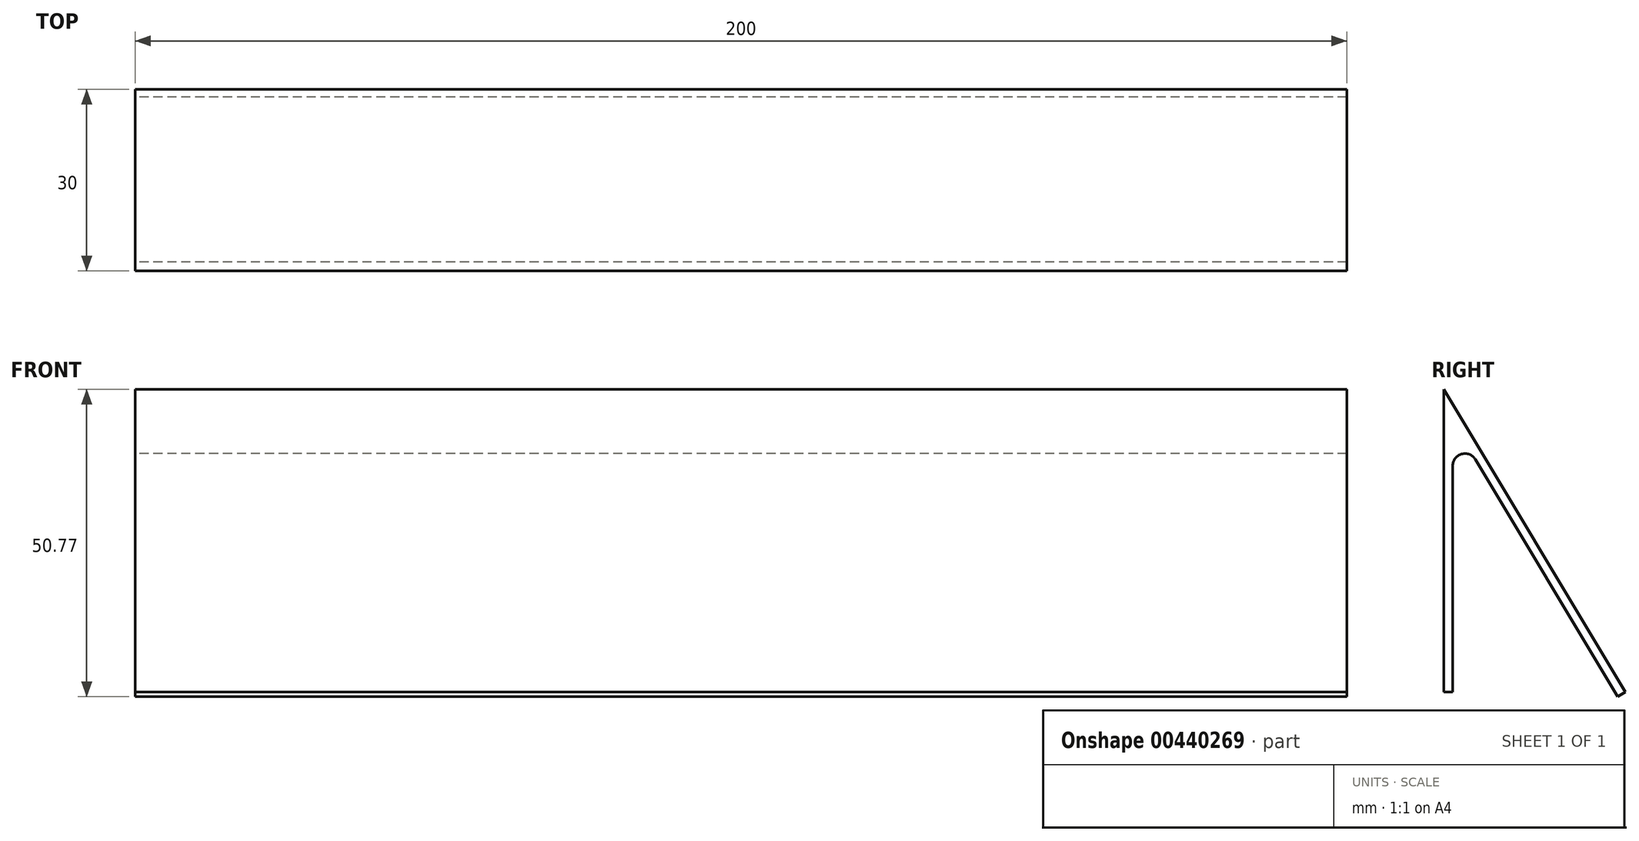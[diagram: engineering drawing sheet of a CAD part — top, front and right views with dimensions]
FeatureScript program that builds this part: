
annotation { "Feature Type Name" : "Feature", "Feature Type Description" : "" }
export const myFeature = defineFeature(function(context is Context, id is Id, definition is map)
    precondition{}
    {
        {
            var Q0;
            Q0=qCreatedBy(makeId("Right.planeOp"),FACE);
            var sketch = newSketch(context, id + "F0", { "sketchPlane" : qUnion([Q0])});
            skLineSegment(sketch, "E0", {"start": v(0, 0) * mm, "end": v(0, 50) * mm});
            skLineSegment(sketch, "E1", {"start": v(30, 0) * mm, "end": v(0, 50) * mm});
            skLineSegment(sketch, "E2.0", {"start": v(1.5, 0) * mm, "end": v(1.5, 37.36) * mm});
            skLineSegment(sketch, "E3.0", {"start": v(28.71, -0.77) * mm, "end": v(5.21, 38.4) * mm});
            skArc(sketch, "E4.filletArc", {"start": v(5.21, 38.4) * mm, "mid": v(2.97, 39.3) * mm, "end": v(1.5, 37.36) * mm});
            skLineSegment(sketch, "E5", {"start": v(0, 0) * mm, "end": v(1.5, 0) * mm});
            skLineSegment(sketch, "E6", {"start": v(28.71, -0.77) * mm, "end": v(30, 0) * mm});
            skSolve(sketch);
        }
        {
            var Q0;
            Q0=makeQuery(id+"F0.imprint","IMPRINT",FACE,{"disambiguationData":[TD([[makeQuery(id+"F0.imprint","IMPRINT",EDGE,{"derivedFrom":sQuery(id+"F0.wireOp",EDGE,"E0")}),-1.0]])]});
            extrude(context, id + "F1", {"entities" : qUnion([Q0]), "endBound" : BoundingType.SYMMETRIC, "depth" : 200 * mm, "offsetDistance" : 25 * mm});
        }
    });
